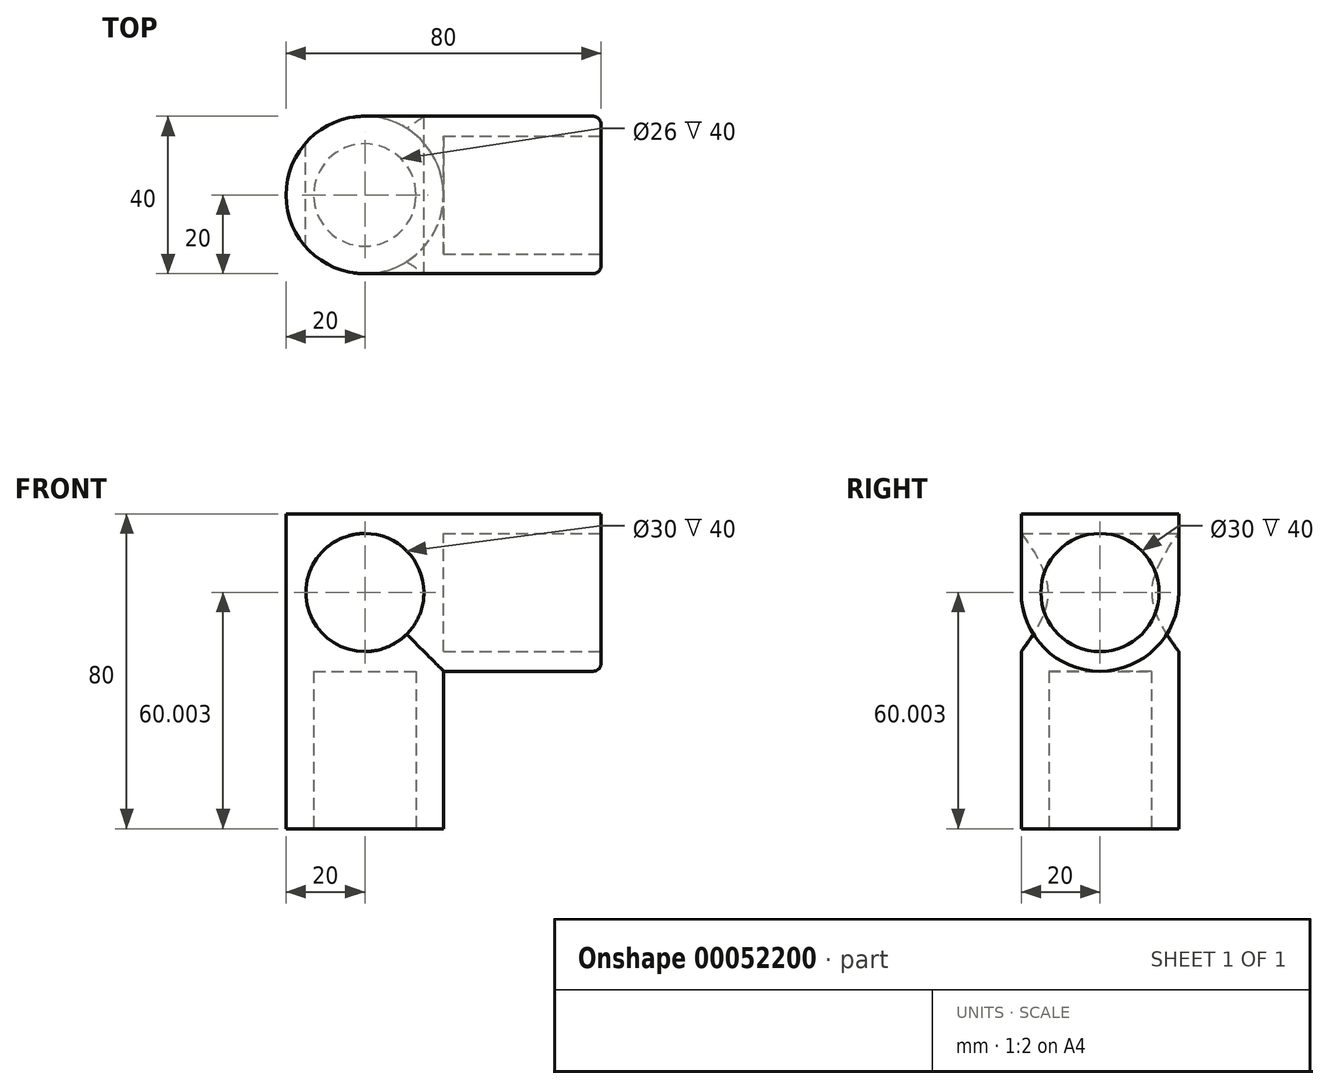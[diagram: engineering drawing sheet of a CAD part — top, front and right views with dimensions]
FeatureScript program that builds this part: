
annotation { "Feature Type Name" : "Feature", "Feature Type Description" : "" }
export const myFeature = defineFeature(function(context is Context, id is Id, definition is map)
    precondition{}
    {
        {
            var Q0;
            Q0=qCreatedBy(makeId("Front.planeOp"),FACE);
            var sketch = newSketch(context, id + "F0", { "sketchPlane" : qUnion([Q0])});
            skLineSegment(sketch, "E0", {"start": v(15, -0.77) * mm, "end": v(15, -40.77) * mm});
            skLineSegment(sketch, "E1", {"start": v(15, -40.77) * mm, "end": v(-25, -40.77) * mm});
            skLineSegment(sketch, "E2", {"start": v(-25, -40.77) * mm, "end": v(-25, 39.23) * mm});
            skLineSegment(sketch, "E3", {"start": v(-25, 39.23) * mm, "end": v(55, 39.23) * mm});
            skLineSegment(sketch, "E4", {"start": v(55, 39.23) * mm, "end": v(55, -0.77) * mm});
            skLineSegment(sketch, "E5", {"start": v(55, -0.77) * mm, "end": v(15, -0.77) * mm});
            skCircle(sketch, "E6", {"center": v(-5, 19.23) * mm, "radius": 15 * mm});
            skSolve(sketch);
        }
        {
            var Q0;
            Q0=makeQuery(id+"F0.imprint","IMPRINT",FACE,{"disambiguationData":[TD([[makeQuery(id+"F0.imprint","IMPRINT",EDGE,{"derivedFrom":sQuery(id+"F0.wireOp",EDGE,"E0")}),-1.0]])]});
            extrude(context, id + "F1", {"entities" : qUnion([Q0]), "depth" : 40 * mm});
        }
        {
            var Q0;
            Q0=makeQuery(id+"F1.opExtrude","SWEPT_FACE",FACE,{"disambiguationData":[OSD([sQuery(id+"F0.wireOp",EDGE,"E1")])]});
            var sketch = newSketch(context, id + "F2", { "sketchPlane" : qUnion([Q0])});
            skCircle(sketch, "E7", {"center": v(-5, 20) * mm, "radius": 13 * mm});
            skSolve(sketch);
        }
        {
            var Q0;
            Q0=makeQuery(id+"F2.imprint","IMPRINT",FACE,{"disambiguationData":[TD([[makeQuery(id+"F2.imprint","IMPRINT",EDGE,{"derivedFrom":sQuery(id+"F2.wireOp",EDGE,"E7")}),1.0]])]});
            var Q1;
            Q1=sQuery(id+"F2.wireOp",EDGE,"E7");
            extrude(context, id + "F3", {"entities" : qUnion([Q0]), "operationType" : NewBodyOperationType.REMOVE, "surfaceEntities" : qUnion([Q1]), "oppositeDirection" : true, "depth" : 40 * mm});
        }
        {
            var Q0;
            Q0=makeQuery(id+"F1.opExtrude","SWEPT_FACE",FACE,{"disambiguationData":[OSD([sQuery(id+"F0.wireOp",EDGE,"E4")])]});
            var sketch = newSketch(context, id + "F4", { "sketchPlane" : qUnion([Q0])});
            skCircle(sketch, "E8", {"center": v(-20, 19.23) * mm, "radius": 15 * mm});
            skSolve(sketch);
        }
        {
            var Q0;
            Q0=makeQuery(id+"F4.imprint","IMPRINT",FACE,{"disambiguationData":[TD([[makeQuery(id+"F4.imprint","IMPRINT",EDGE,{"derivedFrom":sQuery(id+"F4.wireOp",EDGE,"E8")}),1.0]])]});
            extrude(context, id + "F5", {"entities" : qUnion([Q0]), "operationType" : NewBodyOperationType.REMOVE, "oppositeDirection" : true, "depth" : 40 * mm});
        }
        {
            var Q0;
            Q0=makeQuery(id+"F1.opExtrude","CAP_EDGE",EDGE,{"disambiguationData":[OSD([sQuery(id+"F0.wireOp",EDGE,"E0")])],"isStart":true});
            var Q1;
            Q1=makeQuery(id+"F1.opExtrude","CAP_EDGE",EDGE,{"disambiguationData":[OSD([sQuery(id+"F0.wireOp",EDGE,"E0")])],"isStart":false});
            var Q2;
            Q2=makeQuery(id+"F1.opExtrude","CAP_EDGE",EDGE,{"disambiguationData":[OSD([sQuery(id+"F0.wireOp",EDGE,"E2")])],"isStart":false});
            var Q3;
            Q3=makeQuery(id+"F1.opExtrude","CAP_EDGE",EDGE,{"disambiguationData":[OSD([sQuery(id+"F0.wireOp",EDGE,"E2")])],"isStart":true});
            var Q4;
            Q4=makeQuery(id+"F1.opExtrude","CAP_EDGE",EDGE,{"disambiguationData":[OSD([sQuery(id+"F0.wireOp",EDGE,"E5")])],"isStart":true});
            var Q5;
            Q5=makeQuery(id+"F1.opExtrude","CAP_EDGE",EDGE,{"disambiguationData":[OSD([sQuery(id+"F0.wireOp",EDGE,"E5")])],"isStart":false});
            fillet(context, id + "F6", {"entities" : qUnion([Q0, Q1, Q2, Q3, Q4, Q5]), "radius" : 20 * mm, "tangentPropagation" : true, "allowEdgeOverflow" : false});
        }
        {
            var Q0;
            Q0=makeQuery(id+"F1.opExtrude","SWEPT_EDGE",EDGE,{"disambiguationData":[OSD([sQuery(id+"F0.wireOp",EDGE,"E4"),sQuery(id+"F0.wireOp",EDGE,"E5")])]});
            var Q1;
            Q1=makeQuery(id+"F1.opExtrude","SWEPT_EDGE",EDGE,{"disambiguationData":[OSD([sQuery(id+"F0.wireOp",EDGE,"E0"),sQuery(id+"F0.wireOp",EDGE,"E5")])]});
            var Q2;
            Q2=makeQuery(id+"F1.opExtrude","SWEPT_EDGE",EDGE,{"disambiguationData":[OSD([sQuery(id+"F0.wireOp",EDGE,"E0"),sQuery(id+"F0.wireOp",EDGE,"E1")])]});
            var Q3;
            Q3=makeQuery(id+"F1.opExtrude","CAP_EDGE",EDGE,{"disambiguationData":[OSD([sQuery(id+"F0.wireOp",EDGE,"E5")])],"isStart":true});
            var Q4;
            Q4=makeQuery(id+"F1.opExtrude","CAP_EDGE",EDGE,{"disambiguationData":[OSD([sQuery(id+"F0.wireOp",EDGE,"E0")])],"isStart":false});
            var Q5;
            Q5=makeQuery(id+"F1.opExtrude","CAP_EDGE",EDGE,{"disambiguationData":[OSD([sQuery(id+"F0.wireOp",EDGE,"E5")])],"isStart":false});
            var Q6;
            Q6=makeQuery(id+"F1.opExtrude","CAP_EDGE",EDGE,{"disambiguationData":[OSD([sQuery(id+"F0.wireOp",EDGE,"E1")])],"isStart":false});
            var Q7;
            Q7=makeQuery(id+"F1.opExtrude","CAP_EDGE",EDGE,{"disambiguationData":[OSD([sQuery(id+"F0.wireOp",EDGE,"E4")])],"isStart":true});
            var Q8;
            Q8=makeQuery(id+"F1.opExtrude","CAP_EDGE",EDGE,{"disambiguationData":[OSD([sQuery(id+"F0.wireOp",EDGE,"E4")])],"isStart":false});
            var Q9;
            Q9=makeQuery(id+"F1.opExtrude","CAP_EDGE",EDGE,{"disambiguationData":[OSD([sQuery(id+"F0.wireOp",EDGE,"E2")])],"isStart":true});
            var Q10;
            Q10=makeQuery(id+"F1.opExtrude","CAP_EDGE",EDGE,{"disambiguationData":[OSD([sQuery(id+"F0.wireOp",EDGE,"E2")])],"isStart":false});
            var Q11;
            Q11=makeQuery(id+"F1.opExtrude","SWEPT_EDGE",EDGE,{"disambiguationData":[OSD([sQuery(id+"F0.wireOp",EDGE,"E1"),sQuery(id+"F0.wireOp",EDGE,"E2")])]});
            var Q12;
            Q12=makeQuery(id+"F1.opExtrude","CAP_EDGE",EDGE,{"disambiguationData":[OSD([sQuery(id+"F0.wireOp",EDGE,"E1")])],"isStart":true});
            fillet(context, id + "F7", {"entities" : qUnion([Q0, Q1, Q2, Q3, Q4, Q5, Q6, Q7, Q8, Q9, Q10, Q11, Q12]), "radius" : 2 * mm, "tangentPropagation" : true, "allowEdgeOverflow" : false});
        }
    });
